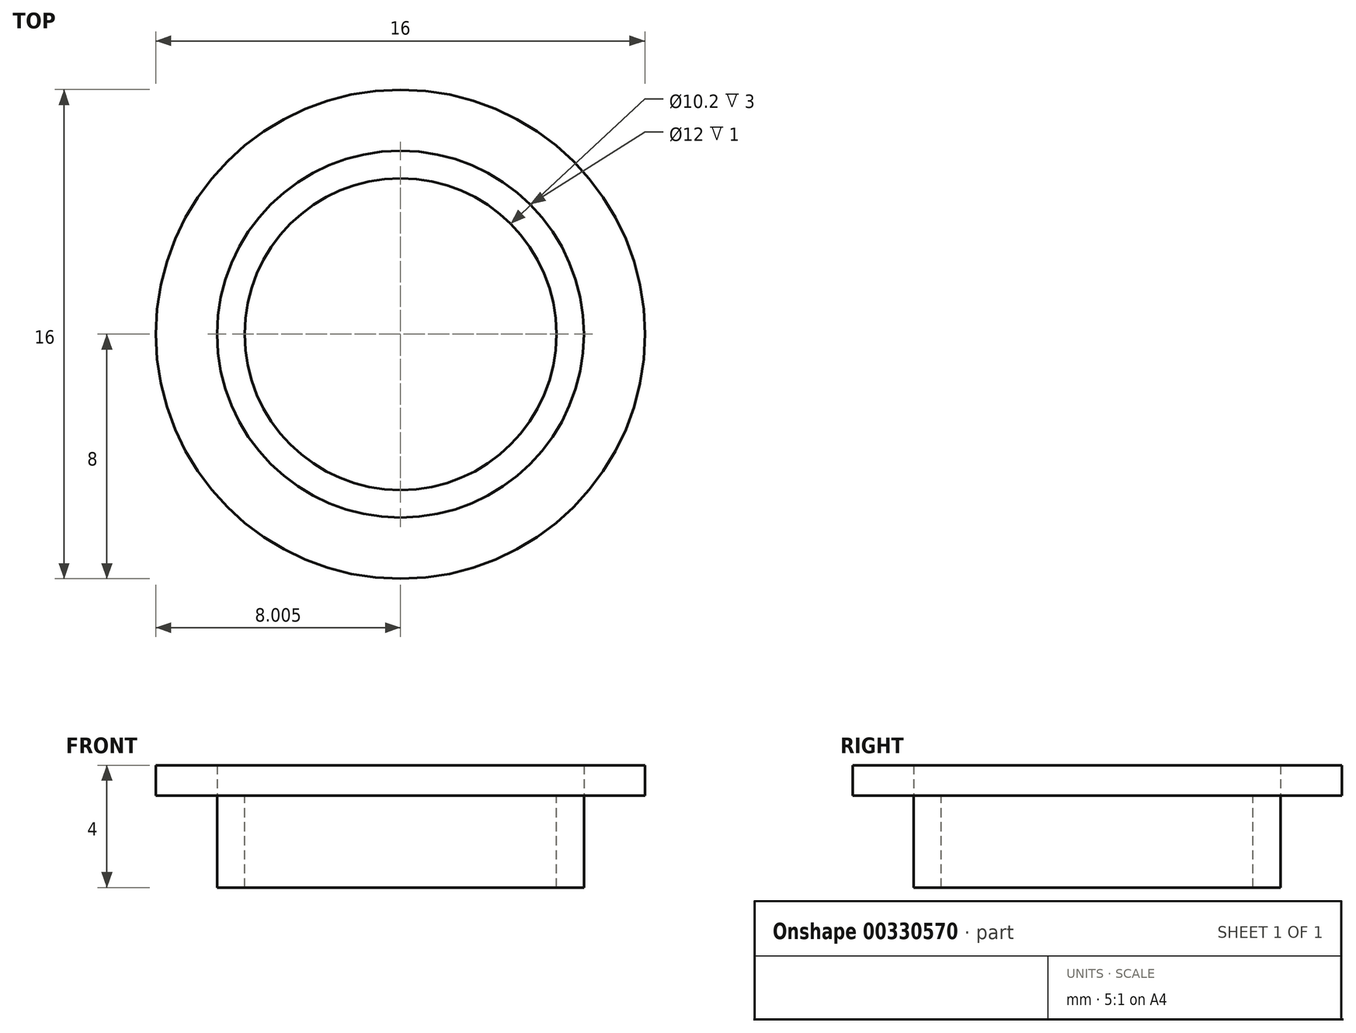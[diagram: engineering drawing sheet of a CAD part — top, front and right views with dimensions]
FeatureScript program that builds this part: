
annotation { "Feature Type Name" : "Feature", "Feature Type Description" : "" }
export const myFeature = defineFeature(function(context is Context, id is Id, definition is map)
    precondition{}
    {
        {
            var Q0;
            Q0=qCreatedBy(makeId("Top.planeOp"),FACE);
            var sketch = newSketch(context, id + "F0", { "sketchPlane" : qUnion([Q0])});
            skCircle(sketch, "E0", {"center": v(-43.95, 40.75) * mm, "radius": 6 * mm});
            skCircle(sketch, "E1", {"center": v(-43.95, 40.75) * mm, "radius": 5.1 * mm});
            skCircle(sketch, "E2.0", {"center": v(-43.95, 40.75) * mm, "radius": 8 * mm});
            skCircle(sketch, "E3", {"center": v(-43.95, 40.75) * mm, "radius": 1.8 * mm});
            skCircle(sketch, "E4", {"center": v(-43.95, 40.75) * mm, "radius": 5.7 * mm});
            skSolve(sketch);
        }
        {
            var Q0;
            Q0 = qSketchRegion(id + "F0", true);
            extrude(context, id + "F1", {"entities" : qUnion([Q0]), "depth" : 1 * mm});
        }
        {
            var Q0;
            Q0=makeQuery(id+"F0.imprint","IMPRINT",FACE,{"disambiguationData":[TD([[makeQuery(id+"F0.imprint","IMPRINT",EDGE,{"derivedFrom":sQuery(id+"F0.wireOp",EDGE,"E0")}),1.0]])]});
            var Q1;
            Q1=makeQuery(id+"F0.imprint","IMPRINT",FACE,{"disambiguationData":[TD([[makeQuery(id+"F0.imprint","IMPRINT",EDGE,{"derivedFrom":sQuery(id+"F0.wireOp",EDGE,"E1")}),-1.0]])]});
            extrude(context, id + "F2", {"entities" : qUnion([Q0, Q1]), "oppositeDirection" : true, "depth" : 3 * mm});
        }
    });
